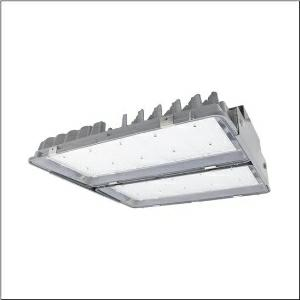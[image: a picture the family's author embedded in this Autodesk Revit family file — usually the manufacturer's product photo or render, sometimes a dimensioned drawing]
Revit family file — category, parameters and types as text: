
# Revit family: highbay_11xtreme_51hf61db4tma
name_source: partatom
category: Lighting Fixtures
units: mm (PartAtom-declared; Revit-internal decimal feet)

## family parameters
Cut with Voids When Loaded = No
Host = Face
Light Source = No
Part Type = Normal
Room Calculation Point = No
Round Connector Dimension = Use Diameter
Shared = No

## types (1)
- --- (1 x LED, 54000 lm, 282.6 W, 4000K)
    Apparent Load = 283 VA
    CIE Flux Codes = 88 96 99 100 100
    Color Rendering = 80
    Color Temperature = 4000K
    Default Elevation = 1800 mm
    Description = Highbay 11Xtreme, high bay luminaire, primary light control with lens, of PMMA, primary optical cover: cover, of toughened safety glass, light emission: direct distribution, primary light characteristic: symmetric, installation type: suspended mounting, surface-mounted, 2x LED module,for 1x 2x LED, rated luminous flux: 54.000lm, luminous efficacy: 191lm/W, light colour: 840, colour temperature: 4000K, control gear: DALI 2, with cable H07RN-F 5x 1.5mm², mains connection: 220..240V, AC, 50/60Hz, cable length: 1,5m, rated input power: 283W, luminaire housing, of diecast aluminium, coated, silver, length: 595mm, width: 560mm, height: 195mm, protection rating (complete): IP66, insulation class (complete): insulation class I (protective earthing), certification: CE, ENEC, UKCA, protection symbol: D, ball protection: ball impact resistant according to DIN VDE 0710 part 13 (with chain suspension), impact resistance: IK08, permissible operating ambient temperature: -25..+60°C, reducing of maximum allowable ambient temperature of 5°C with ceiling mounting, packaging unit: 1 piece
    Height = 157 mm
    Lamp = 1 x LED
    Lamp Light Flux = 54000 lm
    Lamp Power = 282.6 W
    Lamp count = 1
    Length = 593 mm
    Luminous efficacy = 191 lm/W
    Manufacturer = Siteco
    ModVariant = No
    Model = 51HF61DB4TMA
    Mounting Place = Ceiling
    Mounting Type = Pendant
    Number of Poles = 1
    OnlyDefault = Yes
    Power Factor = 1
    Product Name = Highbay 11Xtreme
    Product group = high bay luminaire
    ProductGroupID = 902
    Protection Class = Protection class I
    Protection Degree = IP 66
    RLX_Detail_Level = 1
    RLX_Emergency_Light_Flux = 0 lm
    RLX_Emergency_Type = 0
    RLX_Emergency_Type_DB = No
    RlxData = <blob elided: 33845 chars, md5=42a0a0ca>
    Socket = socket
    Standby Power = 0 W
    System Light Flux = 53999 lm
    System Power = 283 W
    Type Comments = factory setting: luminous flux: 100 % | dim-lin: 254 | 960 mA
    Type Image = l_1258340.jpg
    URL = http://relux.com
    VarID = @adj_088533
    Voltage = 0 V
    Weight = 0.00 kg
    Width = 278 mm

## geometry (parser evidence)
native form markers: Blend x4, Sweep x9
no freeform markers — native parametric forms only
